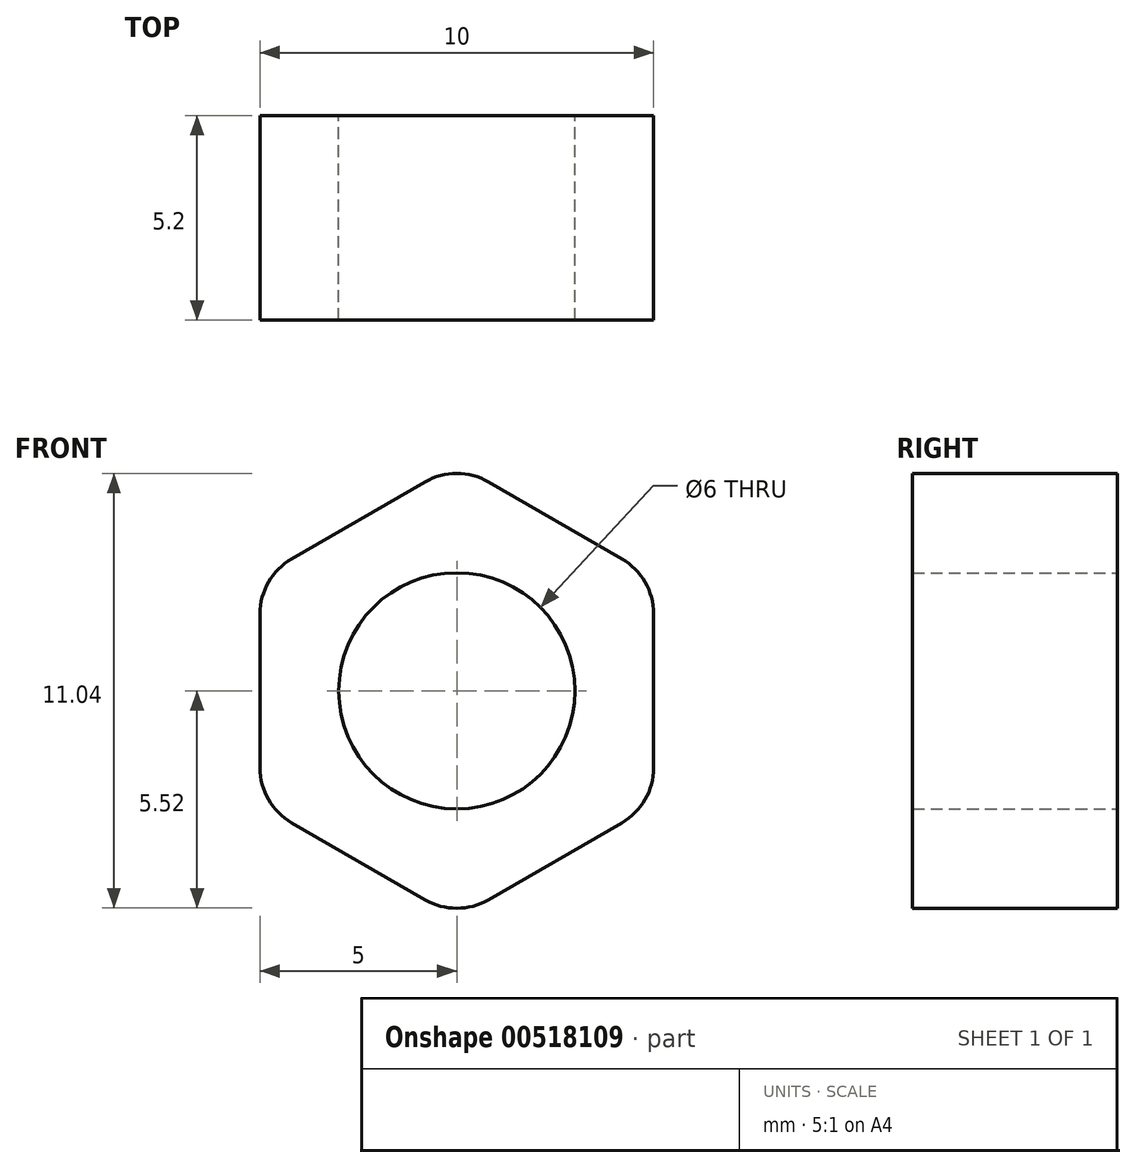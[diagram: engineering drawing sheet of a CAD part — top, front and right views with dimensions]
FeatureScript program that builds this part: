
annotation { "Feature Type Name" : "Feature", "Feature Type Description" : "" }
export const myFeature = defineFeature(function(context is Context, id is Id, definition is map)
    precondition{}
    {
        {
            assignVariable(context, id + "F0", {"name" : "m", "anyValue" : 5.2});
        }
        {
            var Q0;
            Q0=qCreatedBy(makeId("Front.planeOp"),FACE);
            var sketch = newSketch(context, id + "F1", { "sketchPlane" : qUnion([Q0])});
            skLineSegment(sketch, "E0", {"start": v(-0.8, 5.3) * mm, "end": v(-4.2, 3.35) * mm});
            skLineSegment(sketch, "E1", {"start": v(-5, 1.96) * mm, "end": v(-5, -1.96) * mm});
            skLineSegment(sketch, "E2", {"start": v(-4.2, -3.35) * mm, "end": v(-0.8, -5.3) * mm});
            skLineSegment(sketch, "E3", {"start": v(0.8, -5.3) * mm, "end": v(4.2, -3.35) * mm});
            skLineSegment(sketch, "E4", {"start": v(5, -1.96) * mm, "end": v(5, 1.96) * mm});
            skLineSegment(sketch, "E5", {"start": v(4.2, 3.35) * mm, "end": v(0.8, 5.3) * mm});
            skCircle(sketch, "E6", {"center": v(0, 0) * mm, "radius": 3 * mm});
            skLineSegment(sketch, "E7", {"start": v(0, 5.77) * mm, "end": v(0, -5.77) * mm, "construction": true});
            skLineSegment(sketch, "E8", {"start": v(-5, 0) * mm, "end": v(5, 0) * mm, "construction": true});
            skPoint(sketch, "E9.visualSharp", {"position": v(0, 5.77) * mm});
            skArc(sketch, "E9.filletArc", {"start": v(0.8, 5.3) * mm, "mid": v(0, 5.52) * mm, "end": v(-0.8, 5.3) * mm});
            skPoint(sketch, "E10.visualSharp", {"position": v(5, 2.89) * mm});
            skArc(sketch, "E10.filletArc", {"start": v(5, 1.96) * mm, "mid": v(4.78, 2.76) * mm, "end": v(4.2, 3.35) * mm});
            skPoint(sketch, "E11.visualSharp", {"position": v(5, -2.89) * mm});
            skArc(sketch, "E11.filletArc", {"start": v(4.2, -3.35) * mm, "mid": v(4.78, -2.76) * mm, "end": v(5, -1.96) * mm});
            skPoint(sketch, "E12.visualSharp", {"position": v(0, -5.77) * mm});
            skArc(sketch, "E12.filletArc", {"start": v(-0.8, -5.3) * mm, "mid": v(0, -5.52) * mm, "end": v(0.8, -5.3) * mm});
            skPoint(sketch, "E13.visualSharp", {"position": v(-5, -2.89) * mm});
            skArc(sketch, "E13.filletArc", {"start": v(-5, -1.96) * mm, "mid": v(-4.78, -2.76) * mm, "end": v(-4.2, -3.35) * mm});
            skPoint(sketch, "E14.visualSharp", {"position": v(-5, 2.89) * mm});
            skArc(sketch, "E14.filletArc", {"start": v(-4.2, 3.35) * mm, "mid": v(-4.78, 2.76) * mm, "end": v(-5, 1.96) * mm});
            skLineSegment(sketch, "E15", {"start": v(2.5, 4.33) * mm, "end": v(-2.5, -4.33) * mm, "construction": true});
            skSolve(sketch);
        }
        {
            var Q0;
            Q0=makeQuery(id+"F1.imprint","IMPRINT",FACE,{"disambiguationData":[TD([[makeQuery(id+"F1.imprint","IMPRINT",EDGE,{"derivedFrom":sQuery(id+"F1.wireOp",EDGE,"E0")}),1.0]])]});
            extrude(context, id + "F2", {"entities" : qUnion([Q0]), "depth" : (getVariable(context, 'm')) * mm, "offsetDistance" : 25 * mm});
        }
    });
